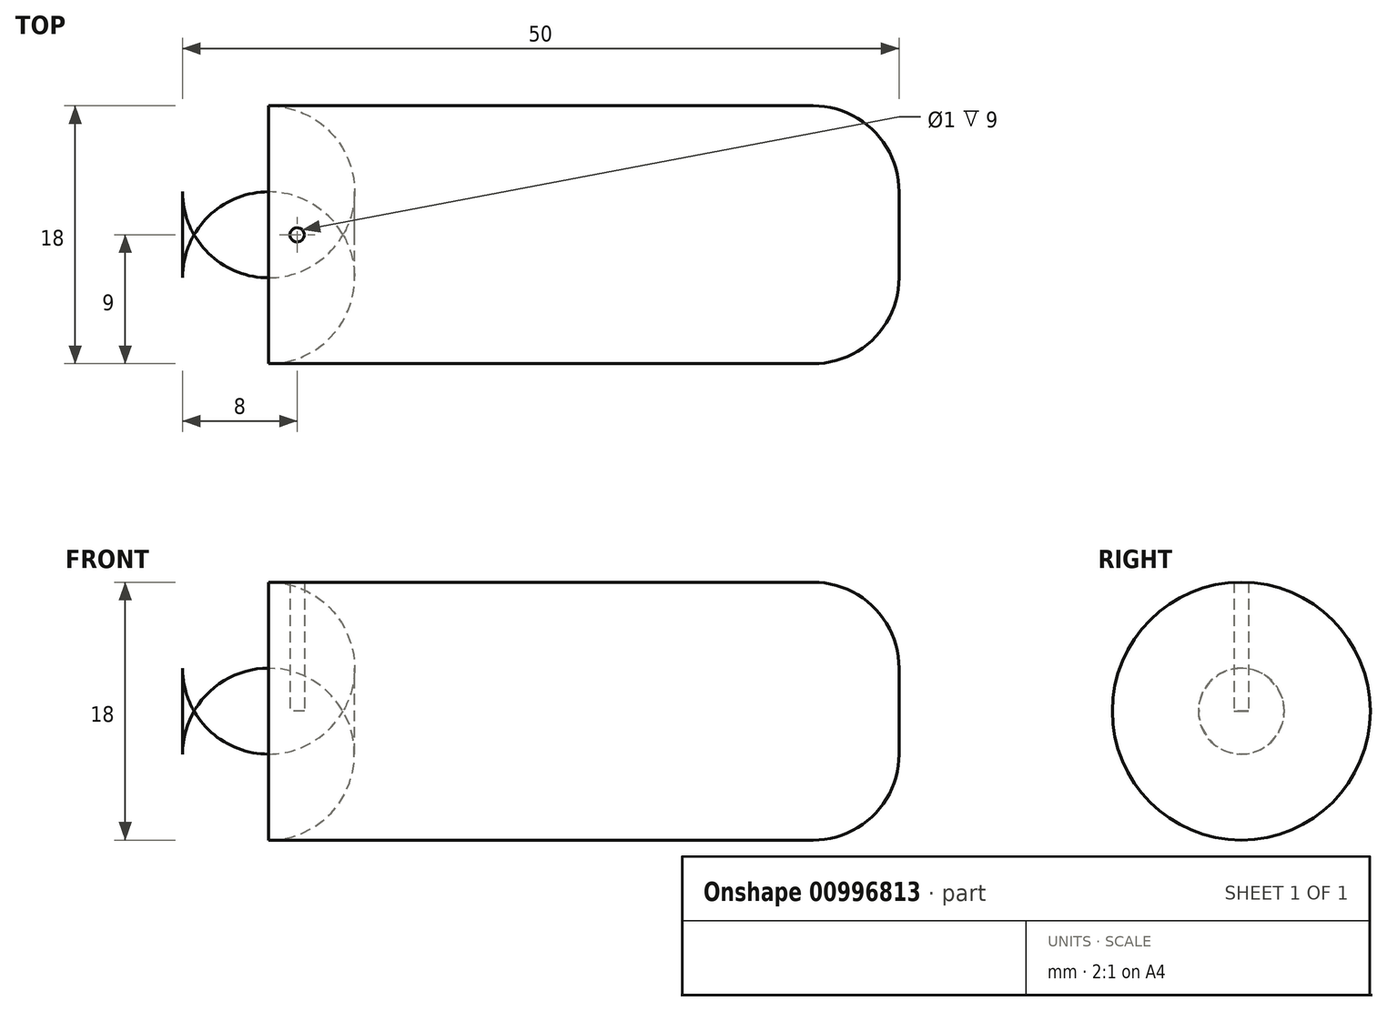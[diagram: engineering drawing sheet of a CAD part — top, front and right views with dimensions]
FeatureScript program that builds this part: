
annotation { "Feature Type Name" : "Feature", "Feature Type Description" : "" }
export const myFeature = defineFeature(function(context is Context, id is Id, definition is map)
    precondition{}
    {
        {
            var Q0;
            Q0=qCreatedBy(makeId("Right.planeOp"),FACE);
            var sketch = newSketch(context, id + "F0", { "sketchPlane" : qUnion([Q0])});
            skCircle(sketch, "E0", {"center": v(0, 0) * mm, "radius": 9 * mm});
            skSolve(sketch);
        }
        {
            var Q0;
            Q0=makeQuery(id+"F0.imprint","IMPRINT",FACE,{"disambiguationData":[TD([[makeQuery(id+"F0.imprint","IMPRINT",EDGE,{"derivedFrom":sQuery(id+"F0.wireOp",EDGE,"E0")}),1.0]])]});
            extrude(context, id + "F1", {"entities" : qUnion([Q0]), "depth" : 50 * mm, "offsetDistance" : 25 * mm});
        }
        {
            var Q0;
            Q0=makeQuery(id+"F1.opExtrude","CAP_EDGE",EDGE,{"disambiguationData":[OSD([sQuery(id+"F0.wireOp",EDGE,"E0")])],"isStart":false});
            var Q1;
            Q1=makeQuery(id+"F1.opExtrude","CAP_EDGE",EDGE,{"disambiguationData":[OSD([sQuery(id+"F0.wireOp",EDGE,"E0")])],"isStart":true});
            fillet(context, id + "F2", {"entities" : qUnion([Q0, Q1]), "radius" : 6 * mm, "tangentPropagation" : true, "allowEdgeOverflow" : false});
        }
        {
            var Q0;
            Q0=qCreatedBy(makeId("Top.planeOp"),FACE);
            var sketch = newSketch(context, id + "F3", { "sketchPlane" : qUnion([Q0])});
            skCircle(sketch, "E1", {"center": v(8, 0) * mm, "radius": 0.5 * mm});
            skSolve(sketch);
        }
        {
            var Q0;
            Q0 = qSketchRegion(id + "F3", true);
            extrude(context, id + "F4", {"entities" : qUnion([Q0]), "operationType" : NewBodyOperationType.REMOVE, "depth" : 25 * mm, "offsetDistance" : 25 * mm});
        }
    });
